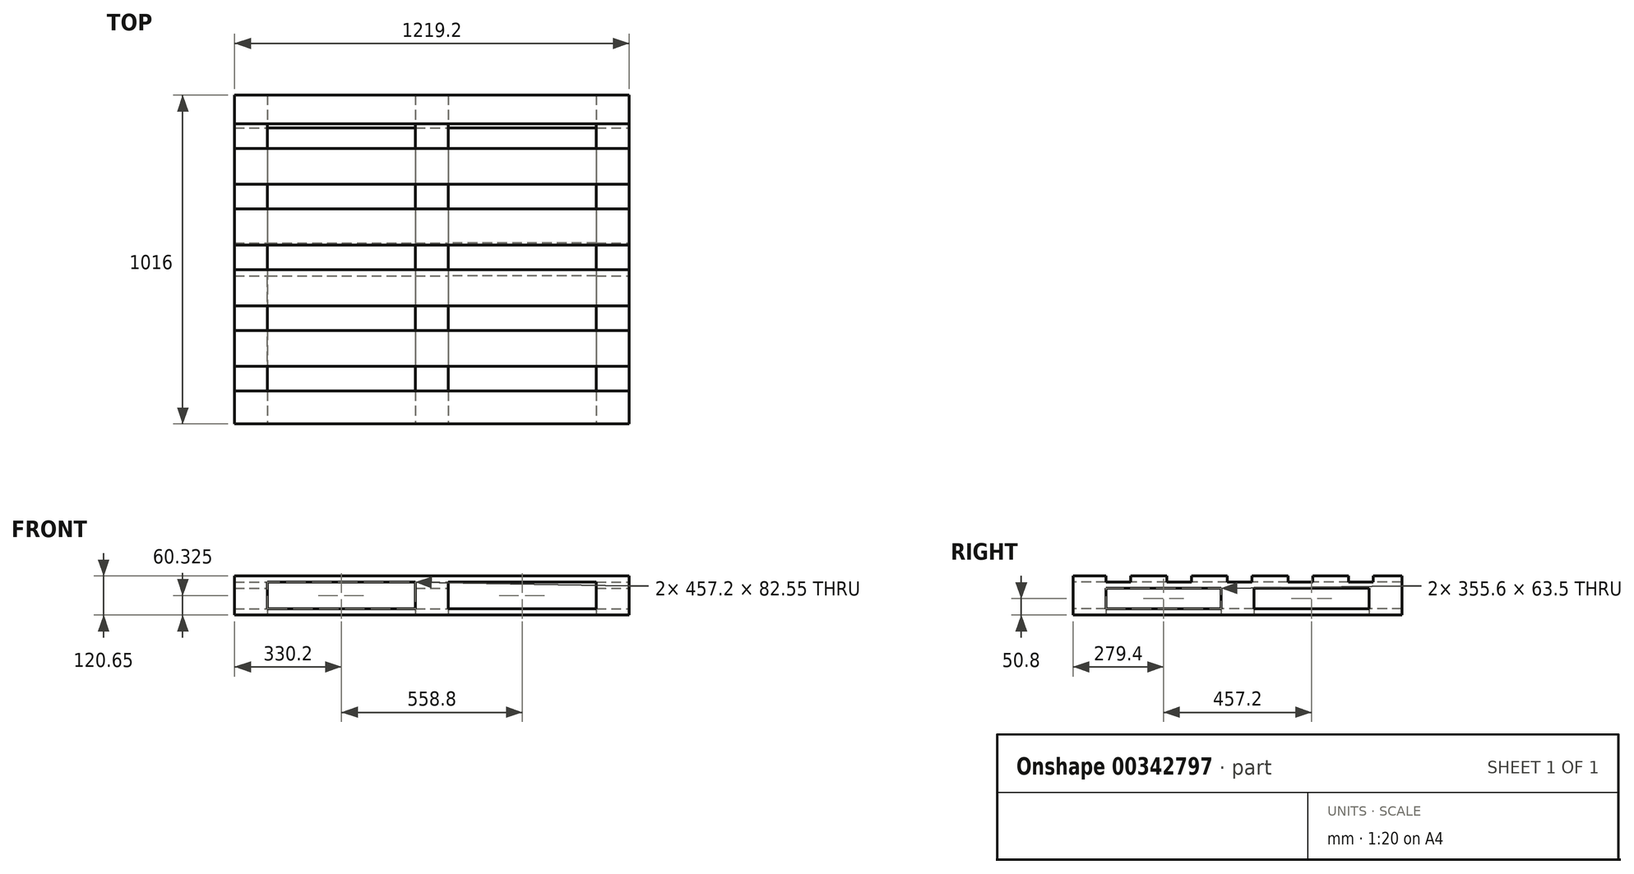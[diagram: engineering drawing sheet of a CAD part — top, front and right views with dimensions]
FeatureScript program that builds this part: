
annotation { "Feature Type Name" : "Feature", "Feature Type Description" : "" }
export const myFeature = defineFeature(function(context is Context, id is Id, definition is map)
    precondition{}
    {
        {
            var Q0;
            Q0=qCreatedBy(makeId("Front.planeOp"),FACE);
            var sketch = newSketch(context, id + "F0", { "sketchPlane" : qUnion([Q0])});
            skLineSegment(sketch, "E0.bottom", {"start": v(609.6, 50.8) * mm, "end": v(-609.6, 50.8) * mm});
            skLineSegment(sketch, "E0.top", {"start": v(609.6, -50.8) * mm, "end": v(-609.6, -50.8) * mm});
            skLineSegment(sketch, "E0.left", {"start": v(609.6, 50.8) * mm, "end": v(609.6, -50.8) * mm});
            skLineSegment(sketch, "E0.right", {"start": v(-609.6, 50.8) * mm, "end": v(-609.6, -50.8) * mm});
            skPoint(sketch, "E0.middle", {"position": v(0, 0) * mm});
            skSolve(sketch);
        }
        {
            var Q0;
            Q0=makeQuery(id+"F0.imprint","IMPRINT",FACE,{"disambiguationData":[TD([[makeQuery(id+"F0.imprint","IMPRINT",EDGE,{"derivedFrom":sQuery(id+"F0.wireOp",EDGE,"E0.bottom")}),1.0]])]});
            extrude(context, id + "F1", {"entities" : qUnion([Q0]), "endBound" : BoundingType.SYMMETRIC, "depth" : 1016 * mm});
        }
        {
            var Q0;
            Q0=makeQuery(id+"F1.opExtrude","CAP_FACE",FACE,{"disambiguationData":[OSD([sQuery(id+"F0.wireOp",EDGE,"E0.bottom"),sQuery(id+"F0.wireOp",EDGE,"E0.top"),sQuery(id+"F0.wireOp",EDGE,"E0.left"),sQuery(id+"F0.wireOp",EDGE,"E0.right")])],"isStart":false});
            var sketch = newSketch(context, id + "F2", { "sketchPlane" : qUnion([Q0])});
            skLineSegment(sketch, "E1.bottom", {"start": v(-50.8, 31.75) * mm, "end": v(-508, 31.75) * mm});
            skLineSegment(sketch, "E1.top", {"start": v(-50.8, -31.75) * mm, "end": v(-508, -31.75) * mm});
            skLineSegment(sketch, "E1.left", {"start": v(-50.8, 31.75) * mm, "end": v(-50.8, -31.75) * mm});
            skLineSegment(sketch, "E1.right", {"start": v(-508, 31.75) * mm, "end": v(-508, -31.75) * mm});
            skPoint(sketch, "E1.middle", {"position": v(-279.4, 0) * mm});
            skLineSegment(sketch, "E2", {"start": v(0, 50.8) * mm, "end": v(0, -50.8) * mm, "construction": true});
            skPoint(sketch, "E3.MirrorP", {"position": v(279.4, 0) * mm});
            skLineSegment(sketch, "E4.MirrorCS", {"start": v(50.8, 31.75) * mm, "end": v(508, 31.75) * mm});
            skLineSegment(sketch, "E5.MirrorCS", {"start": v(50.8, -31.75) * mm, "end": v(508, -31.75) * mm});
            skLineSegment(sketch, "E6.MirrorCS", {"start": v(50.8, 31.75) * mm, "end": v(50.8, -31.75) * mm});
            skLineSegment(sketch, "E7.MirrorCS", {"start": v(508, 31.75) * mm, "end": v(508, -31.75) * mm});
            skSolve(sketch);
        }
        {
            var Q0;
            Q0=qSketchRegion(id+"F2",true);
            extrude(context, id + "F3", {"entities" : qUnion([Q0]), "operationType" : NewBodyOperationType.REMOVE, "endBound" : BoundingType.THROUGH_ALL, "oppositeDirection" : true, "depth" : 25.4 * mm});
        }
        {
            var Q0;
            Q0=makeQuery(id+"F1.opExtrude","SWEPT_FACE",FACE,{"disambiguationData":[OSD([sQuery(id+"F0.wireOp",EDGE,"E0.left")])]});
            var sketch = newSketch(context, id + "F4", { "sketchPlane" : qUnion([Q0])});
            skLineSegment(sketch, "E8.bottom", {"start": v(-406.4, 31.75) * mm, "end": v(-50.8, 31.75) * mm});
            skLineSegment(sketch, "E8.top", {"start": v(-406.4, -31.75) * mm, "end": v(-50.8, -31.75) * mm});
            skLineSegment(sketch, "E8.left", {"start": v(-406.4, 31.75) * mm, "end": v(-406.4, -31.75) * mm});
            skLineSegment(sketch, "E8.right", {"start": v(-50.8, 31.75) * mm, "end": v(-50.8, -31.75) * mm});
            skPoint(sketch, "E8.middle", {"position": v(-228.6, 0) * mm});
            skLineSegment(sketch, "E9", {"start": v(0, 50.8) * mm, "end": v(0, -50.8) * mm, "construction": true});
            skLineSegment(sketch, "E10.MirrorCS", {"start": v(406.4, 31.75) * mm, "end": v(50.8, 31.75) * mm});
            skPoint(sketch, "E11.MirrorP", {"position": v(228.6, 0) * mm});
            skLineSegment(sketch, "E12.MirrorCS", {"start": v(406.4, -31.75) * mm, "end": v(50.8, -31.75) * mm});
            skLineSegment(sketch, "E13.MirrorCS", {"start": v(406.4, 31.75) * mm, "end": v(406.4, -31.75) * mm});
            skLineSegment(sketch, "E14.MirrorCS", {"start": v(50.8, 31.75) * mm, "end": v(50.8, -31.75) * mm});
            skSolve(sketch);
        }
        {
            var Q0;
            Q0=qSketchRegion(id+"F4",true);
            extrude(context, id + "F5", {"entities" : qUnion([Q0]), "operationType" : NewBodyOperationType.REMOVE, "endBound" : BoundingType.THROUGH_ALL, "oppositeDirection" : true, "depth" : 25.4 * mm});
        }
        {
            var Q0;
            Q0=makeQuery(id+"F1.opExtrude","SWEPT_FACE",FACE,{"disambiguationData":[OSD([sQuery(id+"F0.wireOp",EDGE,"E0.top")])]});
            var sketch = newSketch(context, id + "F6", { "sketchPlane" : qUnion([Q0])});
            skLineSegment(sketch, "E15", {"start": v(0, 0) * mm, "end": v(0, 508) * mm, "construction": true});
            skLineSegment(sketch, "E16", {"start": v(0, 0) * mm, "end": v(0, -508) * mm, "construction": true});
            skLineSegment(sketch, "E17", {"start": v(-609.6, 0) * mm, "end": v(609.6, 0) * mm, "construction": true});
            skLineSegment(sketch, "E18.bottom", {"start": v(508, 406.4) * mm, "end": v(50.8, 406.4) * mm});
            skLineSegment(sketch, "E18.top", {"start": v(508, 50.8) * mm, "end": v(50.8, 50.8) * mm});
            skLineSegment(sketch, "E18.left", {"start": v(508, 406.4) * mm, "end": v(508, 50.8) * mm});
            skLineSegment(sketch, "E18.right", {"start": v(50.8, 406.4) * mm, "end": v(50.8, 50.8) * mm});
            skPoint(sketch, "E18.middle", {"position": v(279.4, 228.6) * mm});
            skLineSegment(sketch, "E19.MirrorCS", {"start": v(-508, 50.8) * mm, "end": v(-50.8, 50.8) * mm});
            skLineSegment(sketch, "E20.MirrorCS", {"start": v(-50.8, 406.4) * mm, "end": v(-50.8, 50.8) * mm});
            skLineSegment(sketch, "E21.MirrorCS", {"start": v(-508, 406.4) * mm, "end": v(-50.8, 406.4) * mm});
            skLineSegment(sketch, "E22.MirrorCS", {"start": v(-508, 406.4) * mm, "end": v(-508, 50.8) * mm});
            skLineSegment(sketch, "E23.MirrorCS", {"start": v(508, -406.4) * mm, "end": v(50.8, -406.4) * mm});
            skLineSegment(sketch, "E24.MirrorCS", {"start": v(508, -50.8) * mm, "end": v(50.8, -50.8) * mm});
            skLineSegment(sketch, "E25.MirrorCS", {"start": v(508, -406.4) * mm, "end": v(508, -50.8) * mm});
            skPoint(sketch, "E26.MirrorP", {"position": v(279.4, -228.6) * mm});
            skLineSegment(sketch, "E27.MirrorCS", {"start": v(50.8, -406.4) * mm, "end": v(50.8, -50.8) * mm});
            skLineSegment(sketch, "E28.MirrorCS", {"start": v(-508, -50.8) * mm, "end": v(-50.8, -50.8) * mm});
            skLineSegment(sketch, "E29.MirrorCS", {"start": v(-50.8, -406.4) * mm, "end": v(-50.8, -50.8) * mm});
            skLineSegment(sketch, "E30.MirrorCS", {"start": v(-508, -406.4) * mm, "end": v(-50.8, -406.4) * mm});
            skLineSegment(sketch, "E31.MirrorCS", {"start": v(-508, -406.4) * mm, "end": v(-508, -50.8) * mm});
            skSolve(sketch);
        }
        {
            var Q0;
            Q0=qSketchRegion(id+"F6",true);
            extrude(context, id + "F7", {"entities" : qUnion([Q0]), "operationType" : NewBodyOperationType.REMOVE, "oppositeDirection" : true, "depth" : 25.4 * mm});
        }
        {
            var Q0;
            Q0=makeQuery(id+"F1.opExtrude","CAP_FACE",FACE,{"disambiguationData":[OSD([sQuery(id+"F0.wireOp",EDGE,"E0.bottom"),sQuery(id+"F0.wireOp",EDGE,"E0.top"),sQuery(id+"F0.wireOp",EDGE,"E0.left"),sQuery(id+"F0.wireOp",EDGE,"E0.right")])],"isStart":false});
            var sketch = newSketch(context, id + "F8", { "sketchPlane" : qUnion([Q0])});
            skLineSegment(sketch, "E32.bottom", {"start": v(-508, 50.8) * mm, "end": v(-50.8, 50.8) * mm});
            skLineSegment(sketch, "E32.top", {"start": v(-508, 31.75) * mm, "end": v(-50.8, 31.75) * mm});
            skLineSegment(sketch, "E32.left", {"start": v(-508, 50.8) * mm, "end": v(-508, 31.75) * mm});
            skLineSegment(sketch, "E32.right", {"start": v(-50.8, 50.8) * mm, "end": v(-50.8, 31.75) * mm});
            skLineSegment(sketch, "E33.MirrorCS", {"start": v(508, 50.8) * mm, "end": v(508, 31.75) * mm});
            skLineSegment(sketch, "E34.MirrorCS", {"start": v(50.8, 50.8) * mm, "end": v(50.8, 31.75) * mm});
            skLineSegment(sketch, "E35.MirrorCS", {"start": v(508, 31.75) * mm, "end": v(50.8, 31.75) * mm});
            skLineSegment(sketch, "E36.MirrorCS", {"start": v(508, 50.8) * mm, "end": v(50.8, 50.8) * mm});
            skSolve(sketch);
        }
        {
            var Q0;
            Q0=qSketchRegion(id+"F8",true);
            extrude(context, id + "F9", {"entities" : qUnion([Q0]), "operationType" : NewBodyOperationType.REMOVE, "endBound" : BoundingType.THROUGH_ALL, "oppositeDirection" : true, "depth" : 25.4 * mm});
        }
        {
            var Q0;
            {var subQ0=sQuery(id+"F0.wireOp",EDGE,"E0.left");var subQ3=sQuery(id+"F0.wireOp",EDGE,"E0.bottom");Q0=makeQuery(id+"F9.boolean.opBoolean","SPLIT",FACE,{"disambiguationData":[TD([makeQuery(id+"F1.opExtrude","SWEPT_FACE",FACE,{"disambiguationData":[OSD([subQ0])]})])],"derivedFrom":makeQuery(id+"F1.opExtrude","SWEPT_FACE",FACE,{"disambiguationData":[OSD([subQ3])]})});}
            var sketch = newSketch(context, id + "F10", { "sketchPlane" : qUnion([Q0])});
            skLineSegment(sketch, "E37.bottom", {"start": v(609.6, -508) * mm, "end": v(-609.6, -508) * mm});
            skLineSegment(sketch, "E37.top", {"start": v(609.6, 508) * mm, "end": v(-609.6, 508) * mm});
            skLineSegment(sketch, "E37.left", {"start": v(609.6, -508) * mm, "end": v(609.6, 508) * mm});
            skLineSegment(sketch, "E37.right", {"start": v(-609.6, -508) * mm, "end": v(-609.6, 508) * mm});
            skSolve(sketch);
        }
        {
            var Q0;
            Q0=qSketchRegion(id+"F10",true);
            extrude(context, id + "F11", {"entities" : qUnion([Q0]), "operationType" : NewBodyOperationType.ADD, "depth" : 19.05 * mm});
        }
        {
            var Q0;
            Q0=makeQuery(id+"F11.boolean.opBoolean","MERGE",FACE,{"derivedFrom":[makeQuery(id+"F1.opExtrude","SWEPT_FACE",FACE,{"disambiguationData":[OSD([sQuery(id+"F0.wireOp",EDGE,"E0.left")])]}),makeQuery(id+"F11.opExtrude","SWEPT_FACE",FACE,{"disambiguationData":[OSD([sQuery(id+"F10.wireOp",EDGE,"E37.left")])]})]});
            var sketch = newSketch(context, id + "F12", { "sketchPlane" : qUnion([Q0])});
            skLineSegment(sketch, "E38.bottom", {"start": v(-406.4, 69.85) * mm, "end": v(-330.2, 69.85) * mm});
            skLineSegment(sketch, "E38.top", {"start": v(-406.4, 50.8) * mm, "end": v(-330.2, 50.8) * mm});
            skLineSegment(sketch, "E38.left", {"start": v(-406.4, 69.85) * mm, "end": v(-406.4, 50.8) * mm});
            skLineSegment(sketch, "E38.right", {"start": v(-330.2, 69.85) * mm, "end": v(-330.2, 50.8) * mm});
            skLineSegment(sketch, "E39.1.0.0", {"start": v(-142.75, 69.85) * mm, "end": v(-142.75, 50.8) * mm});
            skLineSegment(sketch, "E39.1.0.1", {"start": v(-218.95, 69.85) * mm, "end": v(-218.95, 50.8) * mm});
            skLineSegment(sketch, "E39.1.0.2", {"start": v(-218.95, 50.8) * mm, "end": v(-142.75, 50.8) * mm});
            skLineSegment(sketch, "E39.1.0.3", {"start": v(-218.95, 69.85) * mm, "end": v(-142.75, 69.85) * mm});
            skLineSegment(sketch, "E39.2.0.0", {"start": v(44.7, 69.85) * mm, "end": v(44.7, 50.8) * mm});
            skLineSegment(sketch, "E39.2.0.1", {"start": v(-31.5, 69.85) * mm, "end": v(-31.5, 50.8) * mm});
            skLineSegment(sketch, "E39.2.0.2", {"start": v(-31.5, 50.8) * mm, "end": v(44.7, 50.8) * mm});
            skLineSegment(sketch, "E39.2.0.3", {"start": v(-31.5, 69.85) * mm, "end": v(44.7, 69.85) * mm});
            skLineSegment(sketch, "E39.3.0.0", {"start": v(232.16, 69.85) * mm, "end": v(232.16, 50.8) * mm});
            skLineSegment(sketch, "E39.3.0.1", {"start": v(155.96, 69.85) * mm, "end": v(155.96, 50.8) * mm});
            skLineSegment(sketch, "E39.3.0.2", {"start": v(155.96, 50.8) * mm, "end": v(232.16, 50.8) * mm});
            skLineSegment(sketch, "E39.3.0.3", {"start": v(155.96, 69.85) * mm, "end": v(232.16, 69.85) * mm});
            skLineSegment(sketch, "E39.4.0.0", {"start": v(419.6, 69.85) * mm, "end": v(419.6, 50.8) * mm});
            skLineSegment(sketch, "E39.4.0.1", {"start": v(343.4, 69.85) * mm, "end": v(343.4, 50.8) * mm});
            skLineSegment(sketch, "E39.4.0.2", {"start": v(343.4, 50.8) * mm, "end": v(419.6, 50.8) * mm});
            skLineSegment(sketch, "E39.4.0.3", {"start": v(343.4, 69.85) * mm, "end": v(419.6, 69.85) * mm});
            skLineSegment(sketch, "E39.5.0.0", {"start": v(607.06, 69.85) * mm, "end": v(607.06, 50.8) * mm});
            skLineSegment(sketch, "E39.5.0.1", {"start": v(530.86, 69.85) * mm, "end": v(530.86, 50.8) * mm});
            skLineSegment(sketch, "E39.5.0.2", {"start": v(530.86, 50.8) * mm, "end": v(607.06, 50.8) * mm});
            skLineSegment(sketch, "E39.5.0.3", {"start": v(530.86, 69.85) * mm, "end": v(607.06, 69.85) * mm});
            skLineSegment(sketch, "E39.direction1", {"start": v(-406.4, 50.8) * mm, "end": v(-218.95, 50.8) * mm, "construction": true});
            skSolve(sketch);
        }
        {
            var Q0;
            Q0=qSketchRegion(id+"F12",true);
            extrude(context, id + "F13", {"entities" : qUnion([Q0]), "operationType" : NewBodyOperationType.REMOVE, "endBound" : BoundingType.THROUGH_ALL, "oppositeDirection" : true, "depth" : 25.4 * mm});
        }
    });
